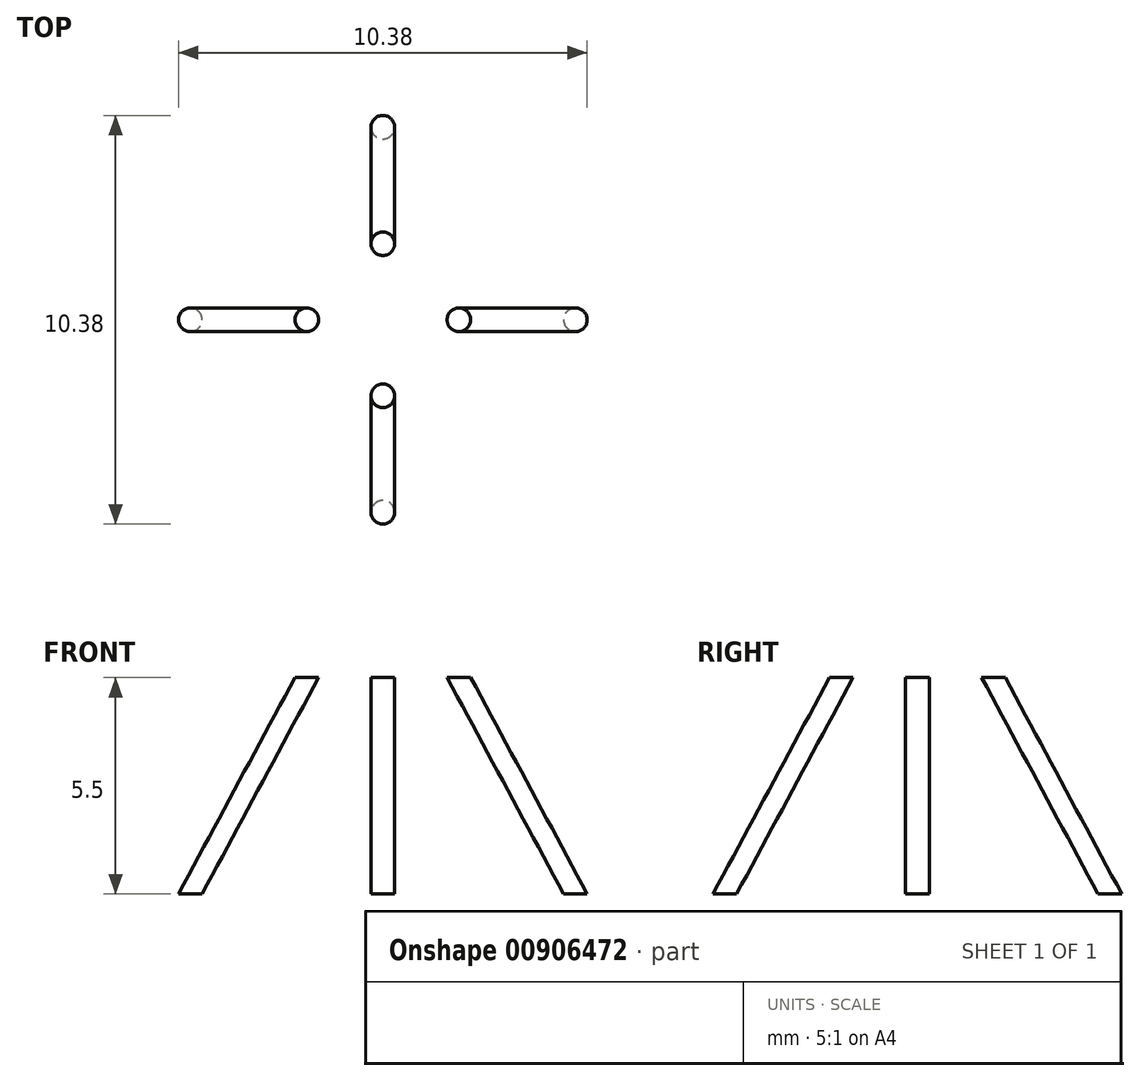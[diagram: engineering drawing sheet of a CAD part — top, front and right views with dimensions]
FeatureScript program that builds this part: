
annotation { "Feature Type Name" : "Feature", "Feature Type Description" : "" }
export const myFeature = defineFeature(function(context is Context, id is Id, definition is map)
    precondition{}
    {
        {
            var Q0;
            Q0=qCreatedBy(makeId("Front.planeOp"),FACE);
            var sketch = newSketch(context, id + "F0", { "sketchPlane" : qUnion([Q0])});
            skLineSegment(sketch, "E0", {"start": v(-1.2, 5.5) * mm, "end": v(-1.6, 5.5) * mm});
            skLineSegment(sketch, "E1", {"start": v(-1.6, 5.5) * mm, "end": v(-4.56, 0) * mm});
            skLineSegment(sketch, "E2", {"start": v(-4.56, 0) * mm, "end": v(-1.2, 0) * mm});
            skLineSegment(sketch, "E3", {"start": v(-1.2, 0) * mm, "end": v(-1.2, 5.5) * mm});
            skLineSegment(sketch, "E4", {"start": v(-1.2, 0) * mm, "end": v(0, 0) * mm, "construction": true});
            skLineSegment(sketch, "E5", {"start": v(0, 0) * mm, "end": v(0, 5.5) * mm, "construction": true});
            skLineSegment(sketch, "E6", {"start": v(0, 5.5) * mm, "end": v(-1.2, 5.5) * mm, "construction": true});
            skSolve(sketch);
        }
        {
            var Q0;
            Q0=makeQuery(id+"F0.imprint","IMPRINT",FACE,{"disambiguationData":[TD([[makeQuery(id+"F0.imprint","IMPRINT",EDGE,{"derivedFrom":sQuery(id+"F0.wireOp",EDGE,"E0")}),1.0]])]});
            var Q1;
            Q1=sQuery(id+"F0.wireOp",EDGE,"E5");
            revolve(context, id + "F1", {"surfaceOperationType" : NewSurfaceOperationType.NEW, "entities" : qUnion([Q0]), "axis" : qUnion([Q1]), "revolveType" : RevolveType.FULL});
        }
        {
            var Q0;
            Q0=qCreatedBy(makeId("Front.planeOp"),FACE);
            var sketch = newSketch(context, id + "F2", { "sketchPlane" : qUnion([Q0])});
            skLineSegment(sketch, "E7", {"start": v(-4.56, 0) * mm, "end": v(-5.46, 0) * mm});
            skLineSegment(sketch, "E8", {"start": v(-5.46, 0) * mm, "end": v(-2.5, 5.5) * mm});
            skLineSegment(sketch, "E9", {"start": v(-2.5, 5.5) * mm, "end": v(-1.6, 5.5) * mm});
            skLineSegment(sketch, "E10", {"start": v(-4.56, 0) * mm, "end": v(-1.6, 5.5) * mm});
            skSolve(sketch);
        }
        {
            var Q0;
            Q0=makeQuery(id+"F2.imprint","IMPRINT",FACE,{"disambiguationData":[TD([[makeQuery(id+"F2.imprint","IMPRINT",EDGE,{"derivedFrom":sQuery(id+"F2.wireOp",EDGE,"E7")}),-1.0]])]});
            extrude(context, id + "F3", {"entities" : qUnion([Q0]), "endBound" : BoundingType.SYMMETRIC, "depth" : 0.9 * mm, "offsetDistance" : 25 * mm});
        }
        {
            var Q0;
            Q0=makeQuery(id+"F3.opExtrude","CAP_EDGE",EDGE,{"disambiguationData":[OSD([sQuery(id+"F2.wireOp",EDGE,"E8")])],"isStart":true});
            var Q1;
            Q1=makeQuery(id+"F3.opExtrude","CAP_EDGE",EDGE,{"disambiguationData":[OSD([sQuery(id+"F2.wireOp",EDGE,"E8")])],"isStart":false});
            fillet(context, id + "F4", {"entities" : qUnion([Q0, Q1]), "radius" : 0.5 * mm, "rho" : 0, "crossSection" : FilletCrossSection.CONIC, "allowEdgeOverflow" : false});
        }
        {
            var Q0;
            Q0=makeQuery(id+"F3.opExtrude","SWEPT_FACE",FACE,{"disambiguationData":[OSD([sQuery(id+"F2.wireOp",EDGE,"E9")])]});
            var sketch = newSketch(context, id + "F5", { "sketchPlane" : qUnion([Q0])});
            skCircle(sketch, "E11", {"center": v(-1.93, 0) * mm, "radius": 0.3 * mm});
            skSolve(sketch);
        }
        {
            var Q0;
            Q0=makeQuery(id+"F3.opExtrude","SWEPT_FACE",FACE,{"disambiguationData":[OSD([sQuery(id+"F2.wireOp",EDGE,"E7")])]});
            var sketch = newSketch(context, id + "F6", { "sketchPlane" : qUnion([Q0])});
            skCircle(sketch, "E12", {"center": v(-4.9, 0) * mm, "radius": 0.3 * mm});
            skSolve(sketch);
        }
        {
            var Q1;
            Q1=makeQuery(id+"F5.imprint","IMPRINT",FACE,{"disambiguationData":[TD([[makeQuery(id+"F5.imprint","IMPRINT",EDGE,{"derivedFrom":sQuery(id+"F5.wireOp",EDGE,"E11")}),1.0]])]});
            var Q2;
            Q2=makeQuery(id+"F6.imprint","IMPRINT",FACE,{"disambiguationData":[TD([[makeQuery(id+"F6.imprint","IMPRINT",EDGE,{"derivedFrom":sQuery(id+"F6.wireOp",EDGE,"E12")}),1.0]])]});
            loft(context, id + "F7", {"sheetProfilesArray" : [{ "sheetProfileEntities" : qUnion([Q1]) }, { "sheetProfileEntities" : qUnion([Q2]) }]});
        }
        {
            var Q0;
            Q0=makeQuery(id+"F3.opExtrude","SWEPT_BODY",BODY,{"disambiguationData":[OSD([sQuery(id+"F2.wireOp",EDGE,"E7"),sQuery(id+"F2.wireOp",EDGE,"E8"),sQuery(id+"F2.wireOp",EDGE,"E9"),sQuery(id+"F2.wireOp",EDGE,"E10")])]});
            var Q1;
            Q1=makeQuery(id+"F1.opRevolve","SWEPT_EDGE",EDGE,{"disambiguationData":[OSD([sQuery(id+"F0.wireOp",EDGE,"E0"),sQuery(id+"F0.wireOp",EDGE,"E1")])]});
            circularPattern(context, id + "F8", {"entities" : qUnion([Q0]), "axis" : qUnion([Q1]), "angle" : 360 * degree, "instanceCount" : 4, "equalSpace" : true});
        }
        {
            var Q0;
            Q0=makeQuery(id+"F7.opLoft","SWEPT_BODY",BODY,{"disambiguationData":[OSD([makeQuery(id+"F5.imprint","IMPRINT",FACE,{"disambiguationData":[TD([[makeQuery(id+"F5.imprint","IMPRINT",EDGE,{"derivedFrom":sQuery(id+"F5.wireOp",EDGE,"E11")}),1.0]])]}),makeQuery(id+"F6.imprint","IMPRINT",FACE,{"disambiguationData":[TD([[makeQuery(id+"F6.imprint","IMPRINT",EDGE,{"derivedFrom":sQuery(id+"F6.wireOp",EDGE,"E12")}),1.0]])]})])]});
            var Q1;
            Q1=makeQuery(id+"F1.opRevolve","SWEPT_EDGE",EDGE,{"disambiguationData":[OSD([sQuery(id+"F0.wireOp",EDGE,"E1"),sQuery(id+"F0.wireOp",EDGE,"E2")])]});
            circularPattern(context, id + "F9", {"entities" : qUnion([Q0]), "axis" : qUnion([Q1]), "angle" : 360 * degree, "instanceCount" : 4, "equalSpace" : true});
        }
        {
            var Q0;
            Q0=makeQuery(id+"F8.opPattern","COPY",BODY,{"derivedFrom":makeQuery(id+"F3.opExtrude","SWEPT_BODY",BODY,{"disambiguationData":[OSD([sQuery(id+"F2.wireOp",EDGE,"E7"),sQuery(id+"F2.wireOp",EDGE,"E8"),sQuery(id+"F2.wireOp",EDGE,"E9"),sQuery(id+"F2.wireOp",EDGE,"E10")])]}),"instanceName":"2"});
            deleteBodies(context, id + "F10", {"entities" : qUnion([Q0])});
        }
        {
            var Q0;
            Q0=makeQuery(id+"F8.opPattern","COPY",BODY,{"derivedFrom":makeQuery(id+"F3.opExtrude","SWEPT_BODY",BODY,{"disambiguationData":[OSD([sQuery(id+"F2.wireOp",EDGE,"E7"),sQuery(id+"F2.wireOp",EDGE,"E8"),sQuery(id+"F2.wireOp",EDGE,"E9"),sQuery(id+"F2.wireOp",EDGE,"E10")])]}),"instanceName":"3"});
            deleteBodies(context, id + "F11", {"entities" : qUnion([Q0])});
        }
        {
            var Q0;
            Q0=makeQuery(id+"F8.opPattern","COPY",BODY,{"derivedFrom":makeQuery(id+"F3.opExtrude","SWEPT_BODY",BODY,{"disambiguationData":[OSD([sQuery(id+"F2.wireOp",EDGE,"E7"),sQuery(id+"F2.wireOp",EDGE,"E8"),sQuery(id+"F2.wireOp",EDGE,"E9"),sQuery(id+"F2.wireOp",EDGE,"E10")])]}),"instanceName":"1"});
            deleteBodies(context, id + "F12", {"entities" : qUnion([Q0])});
        }
        {
            var Q0;
            Q0=makeQuery(id+"F3.opExtrude","SWEPT_BODY",BODY,{"disambiguationData":[OSD([sQuery(id+"F2.wireOp",EDGE,"E7"),sQuery(id+"F2.wireOp",EDGE,"E8"),sQuery(id+"F2.wireOp",EDGE,"E9"),sQuery(id+"F2.wireOp",EDGE,"E10")])]});
            deleteBodies(context, id + "F13", {"entities" : qUnion([Q0])});
        }
        {
            var Q0;
            Q0=makeQuery(id+"F1.opRevolve","SWEPT_BODY",BODY,{"disambiguationData":[OSD([sQuery(id+"F0.wireOp",EDGE,"E0"),sQuery(id+"F0.wireOp",EDGE,"E1"),sQuery(id+"F0.wireOp",EDGE,"E2"),sQuery(id+"F0.wireOp",EDGE,"E3")])]});
            deleteBodies(context, id + "F14", {"entities" : qUnion([Q0])});
        }
    });
